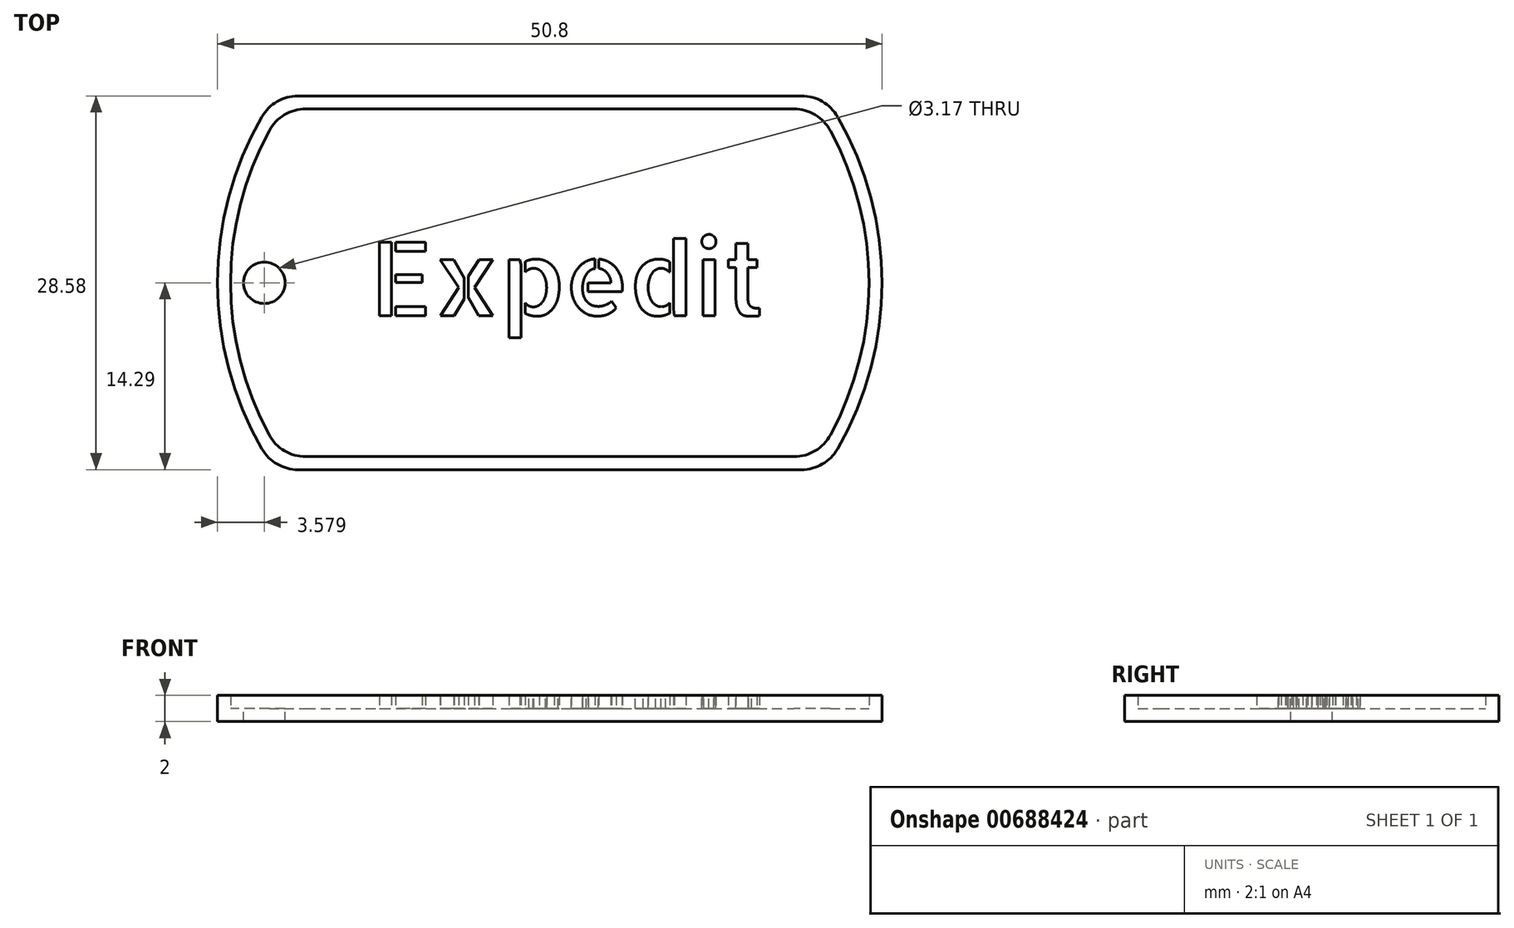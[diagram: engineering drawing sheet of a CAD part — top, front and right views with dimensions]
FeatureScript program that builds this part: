
annotation { "Feature Type Name" : "Feature", "Feature Type Description" : "" }
export const myFeature = defineFeature(function(context is Context, id is Id, definition is map)
    precondition{}
    {
        {
            var Q0;
            Q0=qCreatedBy(makeId("Top.planeOp"),FACE);
            var sketch = newSketch(context, id + "F0", { "sketchPlane" : qUnion([Q0])});
            skArc(sketch, "E0", {"start": v(-22, 12.7) * mm, "mid": v(-25.4, 0) * mm, "end": v(-22, -12.7) * mm});
            skLineSegment(sketch, "E1.top", {"start": v(-19.25, -14.29) * mm, "end": v(19.25, -14.29) * mm});
            skArc(sketch, "E2.trimOffspring", {"start": v(22, -12.7) * mm, "mid": v(25.4, 0) * mm, "end": v(22, 12.7) * mm});
            skLineSegment(sketch, "E3", {"start": v(-19.25, 14.29) * mm, "end": v(19.25, 14.29) * mm});
            skPoint(sketch, "E4.visualSharp", {"position": v(-21, 14.29) * mm});
            skArc(sketch, "E4.filletArc", {"start": v(-19.25, 14.29) * mm, "mid": v(-20.83, 13.86) * mm, "end": v(-22, 12.7) * mm});
            skPoint(sketch, "E5.visualSharp", {"position": v(21, 14.29) * mm});
            skArc(sketch, "E5.filletArc", {"start": v(22, 12.7) * mm, "mid": v(20.83, 13.86) * mm, "end": v(19.25, 14.29) * mm});
            skPoint(sketch, "E6.visualSharp", {"position": v(21, -14.29) * mm});
            skArc(sketch, "E6.filletArc", {"start": v(19.25, -14.29) * mm, "mid": v(20.83, -13.86) * mm, "end": v(22, -12.7) * mm});
            skPoint(sketch, "E7.visualSharp", {"position": v(-21, -14.29) * mm});
            skArc(sketch, "E7.filletArc", {"start": v(-22, -12.7) * mm, "mid": v(-20.83, -13.86) * mm, "end": v(-19.25, -14.29) * mm});
            skSolve(sketch);
        }
        {
            var Q0;
            Q0=makeQuery(id+"F0.imprint","IMPRINT",FACE,{"disambiguationData":[TD([[makeQuery(id+"F0.imprint","IMPRINT",EDGE,{"derivedFrom":sQuery(id+"F0.wireOp",EDGE,"E0")}),1.0]])]});
            extrude(context, id + "F1", {"entities" : qUnion([Q0]), "depth" : 1 * mm, "offsetDistance" : 25.4 * mm});
        }
        {
            var Q0;
            Q0=makeQuery(id+"F1.opExtrude","CAP_FACE",FACE,{"disambiguationData":[OSD([sQuery(id+"F0.wireOp",EDGE,"E0"),sQuery(id+"F0.wireOp",EDGE,"E1.top"),sQuery(id+"F0.wireOp",EDGE,"E2.trimOffspring"),sQuery(id+"F0.wireOp",EDGE,"E3"),sQuery(id+"F0.wireOp",EDGE,"E4.filletArc"),sQuery(id+"F0.wireOp",EDGE,"E5.filletArc"),sQuery(id+"F0.wireOp",EDGE,"E6.filletArc"),sQuery(id+"F0.wireOp",EDGE,"E7.filletArc")])],"isStart":false});
            var sketch = newSketch(context, id + "F2", { "sketchPlane" : qUnion([Q0])});
            skLineSegment(sketch, "E8.0", {"start": v(-18.66, 13.29) * mm, "end": v(18.66, 13.29) * mm});
            skArc(sketch, "E8.1", {"start": v(-21.45, 11.63) * mm, "mid": v(-24.4, 0) * mm, "end": v(-21.45, -11.63) * mm});
            skLineSegment(sketch, "E8.2", {"start": v(-18.66, -13.29) * mm, "end": v(18.66, -13.29) * mm});
            skArc(sketch, "E8.3", {"start": v(21.45, -11.63) * mm, "mid": v(24.4, 0) * mm, "end": v(21.45, 11.63) * mm});
            skPoint(sketch, "E9.visualSharp", {"position": v(-20.46, 13.29) * mm});
            skArc(sketch, "E9.filletArc", {"start": v(-18.66, 13.29) * mm, "mid": v(-20.29, 12.84) * mm, "end": v(-21.45, 11.63) * mm});
            skPoint(sketch, "E10.visualSharp", {"position": v(20.46, 13.29) * mm});
            skArc(sketch, "E10.filletArc", {"start": v(21.45, 11.63) * mm, "mid": v(20.29, 12.84) * mm, "end": v(18.66, 13.29) * mm});
            skPoint(sketch, "E11.visualSharp", {"position": v(20.46, -13.29) * mm});
            skArc(sketch, "E11.filletArc", {"start": v(18.66, -13.29) * mm, "mid": v(20.29, -12.84) * mm, "end": v(21.45, -11.63) * mm});
            skPoint(sketch, "E12.visualSharp", {"position": v(-20.46, -13.29) * mm});
            skArc(sketch, "E12.filletArc", {"start": v(-21.45, -11.63) * mm, "mid": v(-20.29, -12.84) * mm, "end": v(-18.66, -13.29) * mm});
            skLineSegment(sketch, "E13.0", {"start": v(-19.25, 14.29) * mm, "end": v(19.25, 14.29) * mm});
            skArc(sketch, "E13.1", {"start": v(-22, 12.7) * mm, "mid": v(-25.4, 0) * mm, "end": v(-22, -12.7) * mm});
            skLineSegment(sketch, "E13.2", {"start": v(-19.25, -14.29) * mm, "end": v(19.25, -14.29) * mm});
            skArc(sketch, "E13.3", {"start": v(22, -12.7) * mm, "mid": v(25.4, 0) * mm, "end": v(22, 12.7) * mm});
            skPoint(sketch, "E14.visualSharp", {"position": v(-21, -14.29) * mm});
            skArc(sketch, "E14.filletArc", {"start": v(-22, -12.7) * mm, "mid": v(-20.83, -13.86) * mm, "end": v(-19.25, -14.29) * mm});
            skPoint(sketch, "E15.visualSharp", {"position": v(21, -14.29) * mm});
            skArc(sketch, "E15.filletArc", {"start": v(19.25, -14.29) * mm, "mid": v(20.83, -13.86) * mm, "end": v(22, -12.7) * mm});
            skPoint(sketch, "E16.visualSharp", {"position": v(21, 14.29) * mm});
            skArc(sketch, "E16.filletArc", {"start": v(22, 12.7) * mm, "mid": v(20.83, 13.86) * mm, "end": v(19.25, 14.29) * mm});
            skPoint(sketch, "E17.visualSharp", {"position": v(-21, 14.29) * mm});
            skArc(sketch, "E17.filletArc", {"start": v(-19.25, 14.29) * mm, "mid": v(-20.83, 13.86) * mm, "end": v(-22, 12.7) * mm});
            skSolve(sketch);
        }
        {
            var Q0;
            Q0=makeQuery(id+"F2.imprint","IMPRINT",FACE,{"disambiguationData":[TD([[makeQuery(id+"F2.imprint","IMPRINT",EDGE,{"derivedFrom":sQuery(id+"F2.wireOp",EDGE,"E8.0")}),1.0]])]});
            extrude(context, id + "F3", {"entities" : qUnion([Q0]), "operationType" : NewBodyOperationType.ADD, "depth" : 1 * mm, "offsetDistance" : 25.4 * mm});
        }
        {
            var Q0;
            Q0=makeQuery(id+"F1.opExtrude","CAP_FACE",FACE,{"disambiguationData":[OSD([sQuery(id+"F0.wireOp",EDGE,"E0"),sQuery(id+"F0.wireOp",EDGE,"E1.top"),sQuery(id+"F0.wireOp",EDGE,"E2.trimOffspring"),sQuery(id+"F0.wireOp",EDGE,"E3"),sQuery(id+"F0.wireOp",EDGE,"E4.filletArc"),sQuery(id+"F0.wireOp",EDGE,"E5.filletArc"),sQuery(id+"F0.wireOp",EDGE,"E6.filletArc"),sQuery(id+"F0.wireOp",EDGE,"E7.filletArc")])],"isStart":false});
            var sketch = newSketch(context, id + "F4", { "sketchPlane" : qUnion([Q0])});
            skCircle(sketch, "E18", {"center": v(-21.82, 0) * mm, "radius": 1.59 * mm});
            skSolve(sketch);
        }
        {
            var Q0;
            Q0=makeQuery(id+"F4.imprint","IMPRINT",FACE,{"disambiguationData":[TD([[makeQuery(id+"F4.imprint","IMPRINT",EDGE,{"derivedFrom":sQuery(id+"F4.wireOp",EDGE,"E18")}),1.0]])]});
            extrude(context, id + "F5", {"entities" : qUnion([Q0]), "operationType" : NewBodyOperationType.REMOVE, "oppositeDirection" : true, "depth" : 1 * mm, "offsetDistance" : 25.4 * mm});
        }
        {
            var Q0;
            Q0=makeQuery(id+"F2.imprint","IMPRINT",FACE,{"disambiguationData":[TD([[makeQuery(id+"F2.imprint","IMPRINT",EDGE,{"derivedFrom":sQuery(id+"F2.wireOp",EDGE,"E8.0")}),-1.0]])]});
            var sketch = newSketch(context, id + "F6", { "sketchPlane" : qUnion([Q0])});
            skText(sketch, "E19", { "text": "Expedit", "fontName": "AllertaStencil-Regular.ttf"});
            const initialGuessF6  = {"E19": [-0.01375, -0.00252, 1, 0, 0.00562]};
            skSetInitialGuess(sketch, initialGuessF6);
            skSolve(sketch);
        }
        {
            var Q0;
            Q0 = qSketchRegion(id + "F6", true);
            extrude(context, id + "F7", {"entities" : qUnion([Q0]), "operationType" : NewBodyOperationType.ADD, "depth" : 1 * mm, "offsetDistance" : 25.4 * mm});
        }
    });
